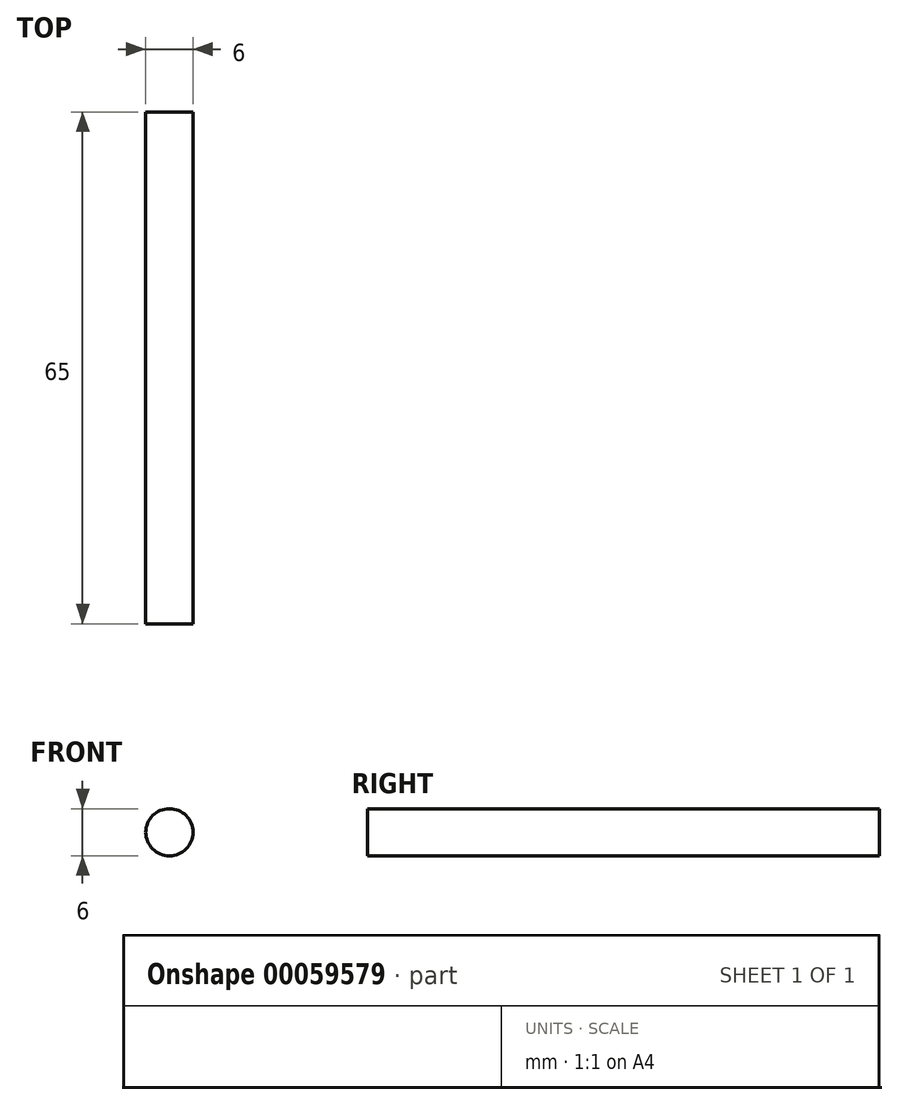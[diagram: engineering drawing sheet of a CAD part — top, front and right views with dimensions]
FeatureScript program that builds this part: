
annotation { "Feature Type Name" : "Feature", "Feature Type Description" : "" }
export const myFeature = defineFeature(function(context is Context, id is Id, definition is map)
    precondition{}
    {
        {
            var Q0;
            Q0=qCreatedBy(makeId("Front.planeOp"),FACE);
            var sketch = newSketch(context, id + "F0", { "sketchPlane" : qUnion([Q0])});
            skCircle(sketch, "E0", {"center": v(0, 0) * mm, "radius": 3 * mm});
            skSolve(sketch);
        }
        {
            var Q0;
            Q0=makeQuery(id+"F0.imprint","IMPRINT",FACE,{"disambiguationData":[TD([[makeQuery(id+"F0.imprint","IMPRINT",EDGE,{"derivedFrom":sQuery(id+"F0.wireOp",EDGE,"E0")}),1.0]])]});
            extrude(context, id + "F1", {"entities" : qUnion([Q0]), "depth" : 65 * mm});
        }
    });
